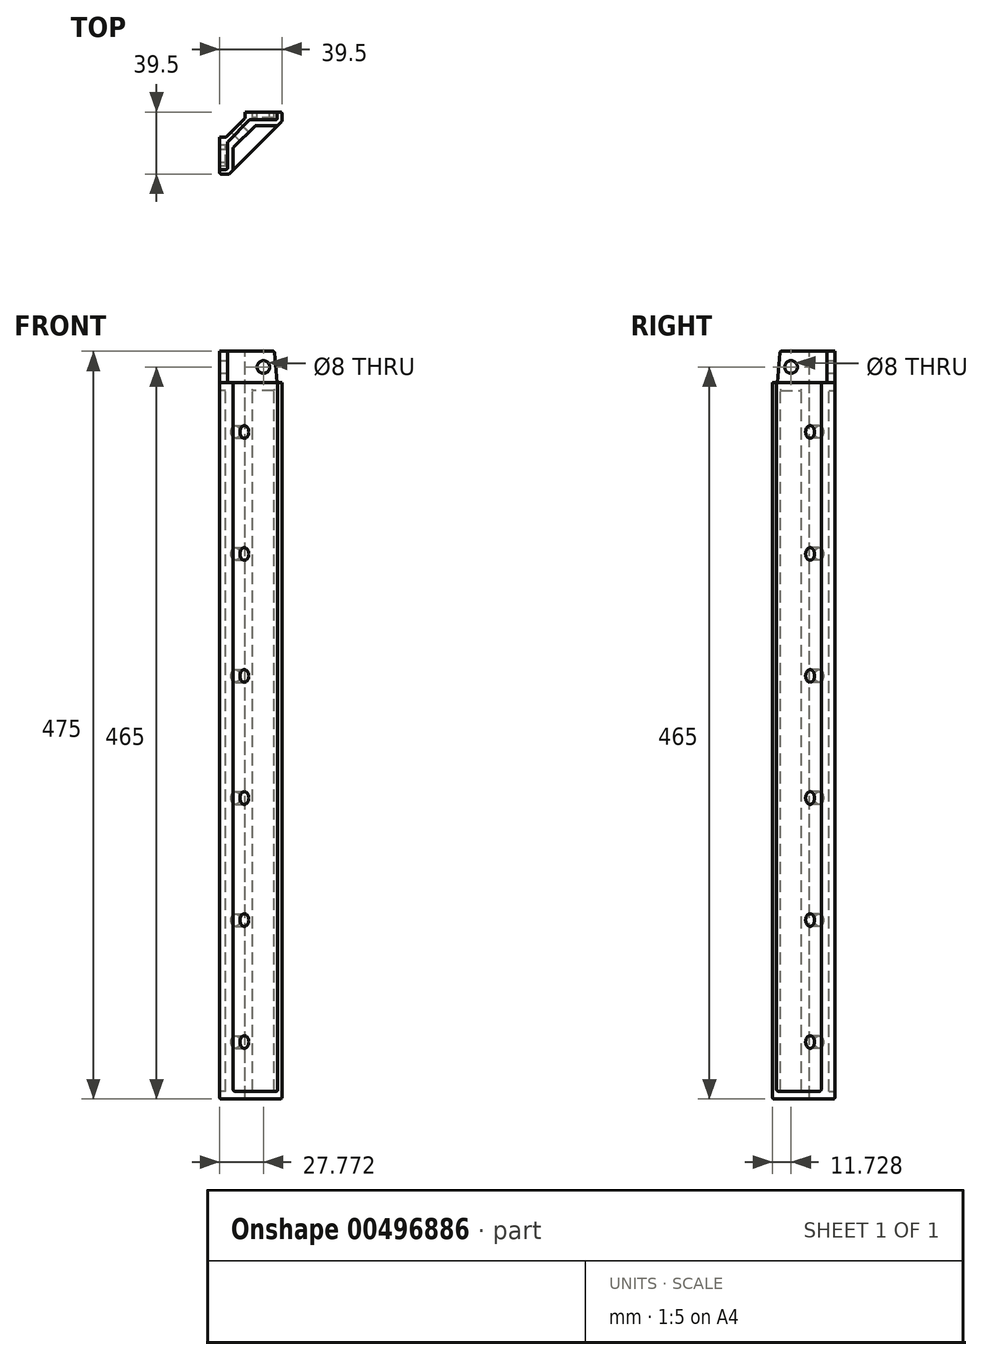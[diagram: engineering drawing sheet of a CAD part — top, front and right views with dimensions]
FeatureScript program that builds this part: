
annotation { "Feature Type Name" : "Feature", "Feature Type Description" : "" }
export const myFeature = defineFeature(function(context is Context, id is Id, definition is map)
    precondition{}
    {
        {
            var Q0;
            Q0=qCreatedBy(makeId("Top.planeOp"),FACE);
            var sketch = newSketch(context, id + "F0", { "sketchPlane" : qUnion([Q0])});
            skLineSegment(sketch, "E0", {"start": v(0, 30.13) * mm, "end": v(0, -27.95) * mm, "construction": true});
            skLineSegment(sketch, "E1", {"start": v(-25.65, 0) * mm, "end": v(27.57, 0) * mm, "construction": true});
            skLineSegment(sketch, "E2.bottom", {"start": v(-19.75, 19.75) * mm, "end": v(19.75, 19.75) * mm});
            skLineSegment(sketch, "E2.top", {"start": v(-19.75, -19.75) * mm, "end": v(-13.75, -19.75) * mm});
            skLineSegment(sketch, "E2.left", {"start": v(-19.75, 19.75) * mm, "end": v(-19.75, -19.75) * mm});
            skLineSegment(sketch, "E2.right", {"start": v(19.75, 19.75) * mm, "end": v(19.75, 13.75) * mm});
            skLineSegment(sketch, "E3", {"start": v(-13.75, -19.75) * mm, "end": v(19.75, 13.75) * mm});
            skSolve(sketch);
        }
        {
            var Q0;
            Q0=qSketchRegion(id+"F0",true);
            extrude(context, id + "F1", {"entities" : qUnion([Q0]), "oppositeDirection" : true, "depth" : 455 * mm, "symmetric" : true});
        }
        {
            var Q0;
            Q0=makeQuery(id+"F1.opExtrude","CAP_FACE",FACE,{"disambiguationData":[OSD([sQuery(id+"F0.wireOp",EDGE,"E2.bottom"),sQuery(id+"F0.wireOp",EDGE,"E2.top"),sQuery(id+"F0.wireOp",EDGE,"E2.left"),sQuery(id+"F0.wireOp",EDGE,"E2.right"),sQuery(id+"F0.wireOp",EDGE,"E3")])],"isStart":true});
            var sketch = newSketch(context, id + "F2", { "sketchPlane" : qUnion([Q0])});
            skLineSegment(sketch, "E4", {"start": v(3, -3) * mm, "end": v(-19.75, 19.75) * mm, "construction": true});
            skLineSegment(sketch, "E5", {"start": v(3, -3) * mm, "end": v(17.14, 11.14) * mm});
            skLineSegment(sketch, "E6", {"start": v(3, -3) * mm, "end": v(-11.14, -17.14) * mm});
            skLineSegment(sketch, "E7", {"start": v(-11.14, -3) * mm, "end": v(3, 11.14) * mm});
            skLineSegment(sketch, "E8", {"start": v(-11.14, -17.14) * mm, "end": v(-11.14, -3) * mm});
            skLineSegment(sketch, "E9", {"start": v(3, 11.14) * mm, "end": v(17.14, 11.14) * mm});
            skSolve(sketch);
        }
        {
            var Q0;
            Q0=qSketchRegion(id+"F2",true);
            extrude(context, id + "F3", {"entities" : qUnion([Q0]), "operationType" : NewBodyOperationType.REMOVE, "oppositeDirection" : true, "depth" : 450 * mm});
        }
        {
            var Q0;
            Q0=makeQuery(id+"F1.opExtrude","CAP_FACE",FACE,{"disambiguationData":[OSD([sQuery(id+"F0.wireOp",EDGE,"E2.bottom"),sQuery(id+"F0.wireOp",EDGE,"E2.top"),sQuery(id+"F0.wireOp",EDGE,"E2.left"),sQuery(id+"F0.wireOp",EDGE,"E2.right"),sQuery(id+"F0.wireOp",EDGE,"E3")])],"isStart":true});
            var sketch = newSketch(context, id + "F4", { "sketchPlane" : qUnion([Q0])});
            skPoint(sketch, "E10.orphan", {"position": v(-19.75, -19.75) * mm});
            skPoint(sketch, "E11.orphan", {"position": v(19.75, 19.75) * mm});
            skLineSegment(sketch, "E12", {"start": v(-19.75, 19.75) * mm, "end": v(-4.07, 4.07) * mm, "construction": true});
            skLineSegment(sketch, "E13", {"start": v(-15.75, 3.7) * mm, "end": v(-19.75, 3.7) * mm});
            skLineSegment(sketch, "E14", {"start": v(-3.7, 15.75) * mm, "end": v(-3.7, 19.75) * mm});
            skLineSegment(sketch, "E15", {"start": v(-3.7, 19.75) * mm, "end": v(-19.75, 19.75) * mm});
            skLineSegment(sketch, "E16", {"start": v(-19.75, 19.75) * mm, "end": v(-19.75, 3.7) * mm});
            skLineSegment(sketch, "E17", {"start": v(-3.7, 15.75) * mm, "end": v(-15.75, 3.7) * mm});
            skPoint(sketch, "E18.orphan", {"position": v(-14.68, 3.7) * mm});
            skPoint(sketch, "E19.orphan", {"position": v(-3.7, 13.6) * mm});
            skSolve(sketch);
        }
        {
            var Q0;
            Q0=qSketchRegion(id+"F4",true);
            extrude(context, id + "F5", {"entities" : qUnion([Q0]), "operationType" : NewBodyOperationType.REMOVE, "endBound" : BoundingType.THROUGH_ALL, "oppositeDirection" : true, "depth" : 25 * mm});
        }
        {
            var Q0;
            Q0=makeQuery(id+"F1.opExtrude","CAP_FACE",FACE,{"disambiguationData":[OSD([sQuery(id+"F0.wireOp",EDGE,"E2.bottom"),sQuery(id+"F0.wireOp",EDGE,"E2.top"),sQuery(id+"F0.wireOp",EDGE,"E2.left"),sQuery(id+"F0.wireOp",EDGE,"E2.right"),sQuery(id+"F0.wireOp",EDGE,"E3")])],"isStart":true});
            var sketch = newSketch(context, id + "F6", { "sketchPlane" : qUnion([Q0])});
            skLineSegment(sketch, "E20.0", {"start": v(1.3, 16.14) * mm, "end": v(14.75, 16.14) * mm});
            skLineSegment(sketch, "E20.1", {"start": v(14.75, 19.75) * mm, "end": v(14.75, 16.14) * mm});
            skLineSegment(sketch, "E21.0", {"start": v(1.3, 16.14) * mm, "end": v(1.3, 19.75) * mm});
            skLineSegment(sketch, "E22", {"start": v(14.75, 19.75) * mm, "end": v(1.3, 19.75) * mm});
            skLineSegment(sketch, "E23.0", {"start": v(-16.14, -14.75) * mm, "end": v(-16.14, -1.3) * mm});
            skLineSegment(sketch, "E23.1", {"start": v(-19.75, -14.75) * mm, "end": v(-16.14, -14.75) * mm});
            skLineSegment(sketch, "E24.0", {"start": v(-16.14, -1.3) * mm, "end": v(-19.75, -1.3) * mm});
            skPoint(sketch, "E25.orphan", {"position": v(-12.53, -1.3) * mm});
            skLineSegment(sketch, "E26", {"start": v(-19.75, -14.75) * mm, "end": v(-19.75, -1.3) * mm});
            skSolve(sketch);
        }
        {
            var Q0;
            Q0=qSketchRegion(id+"F6",true);
            extrude(context, id + "F7", {"entities" : qUnion([Q0]), "operationType" : NewBodyOperationType.REMOVE, "endBound" : BoundingType.THROUGH_ALL, "oppositeDirection" : true, "depth" : 25 * mm});
        }
        {
            var Q0;
            {var subQ1=sQuery(id+"F0.wireOp",EDGE,"E2.right");var subQ4=sQuery(id+"F0.wireOp",EDGE,"E2.bottom");Q0=makeQuery(id+"F7.boolean.opBoolean","SPLIT",FACE,{"disambiguationData":[TD([makeQuery(id+"F1.opExtrude","SWEPT_FACE",FACE,{"disambiguationData":[OSD([subQ1])]})])],"derivedFrom":makeQuery(id+"F1.opExtrude","SWEPT_FACE",FACE,{"disambiguationData":[OSD([subQ4])]})});}
            var sketch = newSketch(context, id + "F8", { "sketchPlane" : qUnion([Q0])});
            skLineSegment(sketch, "E27.bottom", {"start": v(-14.75, 227.5) * mm, "end": v(-1.3, 227.5) * mm});
            skLineSegment(sketch, "E27.top", {"start": v(-14.75, 222.5) * mm, "end": v(-1.3, 222.5) * mm});
            skLineSegment(sketch, "E27.left", {"start": v(-14.75, 227.5) * mm, "end": v(-14.75, 222.5) * mm});
            skLineSegment(sketch, "E27.right", {"start": v(-1.3, 227.5) * mm, "end": v(-1.3, 222.5) * mm});
            skLineSegment(sketch, "E28.bottom", {"start": v(-14.75, -227.5) * mm, "end": v(-1.3, -227.5) * mm});
            skLineSegment(sketch, "E28.top", {"start": v(-14.75, -222.5) * mm, "end": v(-1.3, -222.5) * mm});
            skLineSegment(sketch, "E28.left", {"start": v(-14.75, -227.5) * mm, "end": v(-14.75, -222.5) * mm});
            skLineSegment(sketch, "E28.right", {"start": v(-1.3, -227.5) * mm, "end": v(-1.3, -222.5) * mm});
            skSolve(sketch);
        }
        {
            var Q0;
            Q0=qSketchRegion(id+"F8",true);
            var Q1;
            Q1=makeQuery(id+"F7.boolean.opBoolean","COPY",FACE,{"derivedFrom":makeQuery(id+"F7.opExtrude","SWEPT_FACE",FACE,{"disambiguationData":[OSD([sQuery(id+"F6.wireOp",EDGE,"E20.0")])]})});
            extrude(context, id + "F9", {"entities" : qUnion([Q0]), "operationType" : NewBodyOperationType.ADD, "endBound" : BoundingType.UP_TO_SURFACE, "oppositeDirection" : true, "endBoundEntityFace" : qUnion([Q1]), "depth" : 25 * mm});
        }
        {
            var Q0;
            {var subQ2=sQuery(id+"F0.wireOp",EDGE,"E2.left");var subQ3=sQuery(id+"F0.wireOp",EDGE,"E2.top");Q0=makeQuery(id+"F7.boolean.opBoolean","SPLIT",FACE,{"disambiguationData":[TD([makeQuery(id+"F1.opExtrude","SWEPT_FACE",FACE,{"disambiguationData":[OSD([subQ3])]})])],"derivedFrom":makeQuery(id+"F1.opExtrude","SWEPT_FACE",FACE,{"disambiguationData":[OSD([subQ2])]})});}
            var sketch = newSketch(context, id + "F10", { "sketchPlane" : qUnion([Q0])});
            skLineSegment(sketch, "E29.bottom", {"start": v(14.75, 227.5) * mm, "end": v(1.3, 227.5) * mm});
            skLineSegment(sketch, "E29.top", {"start": v(14.75, 222.5) * mm, "end": v(1.3, 222.5) * mm});
            skLineSegment(sketch, "E29.left", {"start": v(14.75, 227.5) * mm, "end": v(14.75, 222.5) * mm});
            skLineSegment(sketch, "E29.right", {"start": v(1.3, 227.5) * mm, "end": v(1.3, 222.5) * mm});
            skLineSegment(sketch, "E30.bottom", {"start": v(14.75, -227.5) * mm, "end": v(1.3, -227.5) * mm});
            skLineSegment(sketch, "E30.top", {"start": v(14.75, -222.5) * mm, "end": v(1.3, -222.5) * mm});
            skLineSegment(sketch, "E30.left", {"start": v(14.75, -227.5) * mm, "end": v(14.75, -222.5) * mm});
            skLineSegment(sketch, "E30.right", {"start": v(1.3, -227.5) * mm, "end": v(1.3, -222.5) * mm});
            skSolve(sketch);
        }
        {
            var Q0;
            Q0=qSketchRegion(id+"F10",true);
            var Q1;
            Q1=makeQuery(id+"F7.boolean.opBoolean","COPY",FACE,{"derivedFrom":makeQuery(id+"F7.opExtrude","SWEPT_FACE",FACE,{"disambiguationData":[OSD([sQuery(id+"F6.wireOp",EDGE,"E23.0")])]})});
            extrude(context, id + "F11", {"entities" : qUnion([Q0]), "operationType" : NewBodyOperationType.ADD, "endBound" : BoundingType.UP_TO_SURFACE, "oppositeDirection" : true, "endBoundEntityFace" : qUnion([Q1]), "depth" : 25 * mm});
        }
        {
            var Q0;
            {var subQ2=sQuery(id+"F0.wireOp",EDGE,"E2.left");var subQ3=sQuery(id+"F0.wireOp",EDGE,"E2.top");var subQ7=makeQuery(id+"F1.opExtrude","SWEPT_FACE",FACE,{"disambiguationData":[OSD([subQ2])]});Q0=makeQuery(id+"F11.boolean.opBoolean","MERGE",FACE,{"derivedFrom":[makeQuery(id+"F7.boolean.opBoolean","SPLIT",FACE,{"disambiguationData":[TD([makeQuery(id+"F1.opExtrude","SWEPT_FACE",FACE,{"disambiguationData":[OSD([subQ3])]})])],"derivedFrom":subQ7}),makeQuery(id+"F7.boolean.opBoolean","SPLIT",FACE,{"disambiguationData":[TD([makeQuery(id+"F5.boolean.opBoolean","COPY",FACE,{"derivedFrom":makeQuery(id+"F5.opExtrude","SWEPT_FACE",FACE,{"disambiguationData":[OSD([sQuery(id+"F4.wireOp",EDGE,"E13")])]})})])],"derivedFrom":subQ7}),makeQuery(id+"F11.opExtrude","CAP_FACE",FACE,{"disambiguationData":[OSD([sQuery(id+"F10.wireOp",EDGE,"E29.bottom"),sQuery(id+"F10.wireOp",EDGE,"E29.top"),sQuery(id+"F10.wireOp",EDGE,"E29.left"),sQuery(id+"F10.wireOp",EDGE,"E29.right")])],"isStart":true}),makeQuery(id+"F11.opExtrude","CAP_FACE",FACE,{"disambiguationData":[OSD([sQuery(id+"F10.wireOp",EDGE,"E30.bottom"),sQuery(id+"F10.wireOp",EDGE,"E30.top"),sQuery(id+"F10.wireOp",EDGE,"E30.left"),sQuery(id+"F10.wireOp",EDGE,"E30.right")])],"isStart":true})]});}
            var sketch = newSketch(context, id + "F12", { "sketchPlane" : qUnion([Q0])});
            skLineSegment(sketch, "E31", {"start": v(8.02, 227.5) * mm, "end": v(8.02, 247.5) * mm, "construction": true});
            skLineSegment(sketch, "E32", {"start": v(0, 0) * mm, "end": v(35.4, 0) * mm, "construction": true});
            skPoint(sketch, "E32.endSnap0", {"position": v(19.75, 0) * mm});
            skLineSegment(sketch, "E33.MirrorCS", {"start": v(16.04, 0) * mm, "end": v(-19.35, 0) * mm, "construction": true});
            skLineSegment(sketch, "E34", {"start": v(16.75, 227.5) * mm, "end": v(-0.7, 227.5) * mm});
            skLineSegment(sketch, "E35", {"start": v(16.75, 227.5) * mm, "end": v(15.02, 247.5) * mm});
            skLineSegment(sketch, "E36", {"start": v(15.02, 247.5) * mm, "end": v(8.02, 247.5) * mm});
            skLineSegment(sketch, "E37", {"start": v(8.02, 247.5) * mm, "end": v(1.02, 247.5) * mm});
            skLineSegment(sketch, "E38", {"start": v(1.02, 247.5) * mm, "end": v(-0.7, 227.5) * mm});
            skLineSegment(sketch, "E39.MirrorCS", {"start": v(-0.7, 227.5) * mm, "end": v(1.02, 247.5) * mm});
            skSolve(sketch);
        }
        {
            var Q0;
            Q0=qSketchRegion(id+"F12",true);
            extrude(context, id + "F13", {"entities" : qUnion([Q0]), "operationType" : NewBodyOperationType.ADD, "oppositeDirection" : true, "depth" : 5 * mm});
        }
        {
            var Q0;
            {var subQ1=sQuery(id+"F0.wireOp",EDGE,"E2.right");var subQ4=sQuery(id+"F0.wireOp",EDGE,"E2.bottom");var subQ7=makeQuery(id+"F1.opExtrude","SWEPT_FACE",FACE,{"disambiguationData":[OSD([subQ4])]});Q0=makeQuery(id+"F9.boolean.opBoolean","MERGE",FACE,{"derivedFrom":[makeQuery(id+"F7.boolean.opBoolean","SPLIT",FACE,{"disambiguationData":[TD([makeQuery(id+"F1.opExtrude","SWEPT_FACE",FACE,{"disambiguationData":[OSD([subQ1])]})])],"derivedFrom":subQ7}),makeQuery(id+"F7.boolean.opBoolean","SPLIT",FACE,{"disambiguationData":[TD([makeQuery(id+"F5.boolean.opBoolean","COPY",FACE,{"derivedFrom":makeQuery(id+"F5.opExtrude","SWEPT_FACE",FACE,{"disambiguationData":[OSD([sQuery(id+"F4.wireOp",EDGE,"E14")])]})})])],"derivedFrom":subQ7}),makeQuery(id+"F9.opExtrude","CAP_FACE",FACE,{"disambiguationData":[OSD([sQuery(id+"F8.wireOp",EDGE,"E27.bottom"),sQuery(id+"F8.wireOp",EDGE,"E27.top"),sQuery(id+"F8.wireOp",EDGE,"E27.left"),sQuery(id+"F8.wireOp",EDGE,"E27.right")])],"isStart":true}),makeQuery(id+"F9.opExtrude","CAP_FACE",FACE,{"disambiguationData":[OSD([sQuery(id+"F8.wireOp",EDGE,"E28.bottom"),sQuery(id+"F8.wireOp",EDGE,"E28.top"),sQuery(id+"F8.wireOp",EDGE,"E28.left"),sQuery(id+"F8.wireOp",EDGE,"E28.right")])],"isStart":true})]});}
            var sketch = newSketch(context, id + "F14", { "sketchPlane" : qUnion([Q0])});
            skLineSegment(sketch, "E40", {"start": v(-8.02, 227.5) * mm, "end": v(-8.02, 247.66) * mm, "construction": true});
            skPoint(sketch, "E40.endSnap0", {"position": v(-8.02, 227.5) * mm});
            skLineSegment(sketch, "E41", {"start": v(-15.02, 247.5) * mm, "end": v(-1.02, 247.5) * mm});
            skLineSegment(sketch, "E42", {"start": v(0, 0) * mm, "end": v(-60.6, 0) * mm, "construction": true});
            skPoint(sketch, "E42.endSnap0", {"position": v(-14.75, 0) * mm});
            skLineSegment(sketch, "E43", {"start": v(-15.02, 247.5) * mm, "end": v(-16.75, 227.5) * mm});
            skLineSegment(sketch, "E44", {"start": v(-1.02, 247.5) * mm, "end": v(0.7, 227.5) * mm});
            skLineSegment(sketch, "E45", {"start": v(0.7, 227.5) * mm, "end": v(-16.75, 227.5) * mm});
            skSolve(sketch);
        }
        {
            var Q0;
            Q0=qSketchRegion(id+"F14",true);
            extrude(context, id + "F15", {"entities" : qUnion([Q0]), "operationType" : NewBodyOperationType.ADD, "oppositeDirection" : true, "depth" : 5 * mm});
        }
        {
            var Q0;
            {var subQ1=sQuery(id+"F0.wireOp",EDGE,"E2.right");var subQ4=sQuery(id+"F0.wireOp",EDGE,"E2.bottom");var subQ7=makeQuery(id+"F1.opExtrude","SWEPT_FACE",FACE,{"disambiguationData":[OSD([subQ4])]});Q0=makeQuery(id+"F15.boolean.opBoolean","MERGE",FACE,{"derivedFrom":[makeQuery(id+"F9.boolean.opBoolean","MERGE",FACE,{"derivedFrom":[makeQuery(id+"F7.boolean.opBoolean","SPLIT",FACE,{"disambiguationData":[TD([makeQuery(id+"F1.opExtrude","SWEPT_FACE",FACE,{"disambiguationData":[OSD([subQ1])]})])],"derivedFrom":subQ7}),makeQuery(id+"F7.boolean.opBoolean","SPLIT",FACE,{"disambiguationData":[TD([makeQuery(id+"F5.boolean.opBoolean","COPY",FACE,{"derivedFrom":makeQuery(id+"F5.opExtrude","SWEPT_FACE",FACE,{"disambiguationData":[OSD([sQuery(id+"F4.wireOp",EDGE,"E14")])]})})])],"derivedFrom":subQ7}),makeQuery(id+"F9.opExtrude","CAP_FACE",FACE,{"disambiguationData":[OSD([sQuery(id+"F8.wireOp",EDGE,"E27.bottom"),sQuery(id+"F8.wireOp",EDGE,"E27.top"),sQuery(id+"F8.wireOp",EDGE,"E27.left"),sQuery(id+"F8.wireOp",EDGE,"E27.right")])],"isStart":true}),makeQuery(id+"F9.opExtrude","CAP_FACE",FACE,{"disambiguationData":[OSD([sQuery(id+"F8.wireOp",EDGE,"E28.bottom"),sQuery(id+"F8.wireOp",EDGE,"E28.top"),sQuery(id+"F8.wireOp",EDGE,"E28.left"),sQuery(id+"F8.wireOp",EDGE,"E28.right")])],"isStart":true})]}),makeQuery(id+"F15.opExtrude","CAP_FACE",FACE,{"disambiguationData":[OSD([sQuery(id+"F14.wireOp",EDGE,"AjdLOBUI-PND2-HRux-vW9i-I60BuJFxOAxo"),sQuery(id+"F14.wireOp",EDGE,"m2E0O1S7-ugW4-w8lP-xUBK-8UGrL3XVD3p1"),sQuery(id+"F14.wireOp",EDGE,"E41"),sQuery(id+"F14.wireOp",EDGE,"z751VbyZ-Eswl-sp4i-D6d8-2ebrKqnJ25gN")])],"isStart":true}),makeQuery(id+"F15.opExtrude","CAP_FACE",FACE,{"disambiguationData":[OSD([sQuery(id+"F14.wireOp",EDGE,"9fced805-f766-4b14-a849-f1590210c0c81.MirrorCS"),sQuery(id+"F14.wireOp",EDGE,"9fced805-f766-4b14-a849-f1590210c0c82.MirrorCS"),sQuery(id+"F14.wireOp",EDGE,"9fced805-f766-4b14-a849-f1590210c0c83.MirrorCS"),sQuery(id+"F14.wireOp",EDGE,"9fced805-f766-4b14-a849-f1590210c0c84.MirrorCS")])],"isStart":true})]});}
            var sketch = newSketch(context, id + "F16", { "sketchPlane" : qUnion([Q0])});
            skLineSegment(sketch, "E46", {"start": v(-8.02, 247.5) * mm, "end": v(-8.02, 8.86) * mm, "construction": true});
            skCircle(sketch, "E47", {"center": v(-8.02, 237.5) * mm, "radius": 4 * mm});
            skSolve(sketch);
        }
        {
            var Q0;
            Q0=qSketchRegion(id+"F16",true);
            extrude(context, id + "F17", {"entities" : qUnion([Q0]), "operationType" : NewBodyOperationType.REMOVE, "endBound" : BoundingType.THROUGH_ALL, "oppositeDirection" : true, "depth" : 25 * mm});
        }
        {
            var Q0;
            Q0=makeQuery(id+"F3.boolean.opBoolean","COPY",FACE,{"derivedFrom":makeQuery(id+"F3.opExtrude","SWEPT_FACE",FACE,{"disambiguationData":[OSD([sQuery(id+"F2.wireOp",EDGE,"E7")])]})});
            var sketch = newSketch(context, id + "F18", { "sketchPlane" : qUnion([Q0])});
            skLineSegment(sketch, "E48", {"start": v(0, 227.5) * mm, "end": v(0, -222.5) * mm, "construction": true});
            skLineSegment(sketch, "E49", {"start": v(0, 2.5) * mm, "end": v(10, 2.5) * mm, "construction": true});
            skCircle(sketch, "E50", {"center": v(0, 196.25) * mm, "radius": 4 * mm});
            skCircle(sketch, "E51", {"center": v(0, 118.75) * mm, "radius": 4 * mm});
            skCircle(sketch, "E52.MirrorC", {"center": v(0, -191.25) * mm, "radius": 4 * mm});
            skCircle(sketch, "E53.MirrorC", {"center": v(0, -113.75) * mm, "radius": 4 * mm});
            skCircle(sketch, "E54", {"center": v(0, 41.25) * mm, "radius": 4 * mm});
            skCircle(sketch, "E55.MirrorC", {"center": v(0, -36.25) * mm, "radius": 4 * mm});
            skSolve(sketch);
        }
        {
            var Q0;
            Q0=qSketchRegion(id+"F18",true);
            extrude(context, id + "F19", {"entities" : qUnion([Q0]), "operationType" : NewBodyOperationType.REMOVE, "endBound" : BoundingType.THROUGH_ALL, "oppositeDirection" : true, "depth" : 25 * mm});
        }
        {
            var Q0;
            Q0=makeQuery(id+"F13.opExtrude","CAP_FACE",FACE,{"disambiguationData":[OSD([sQuery(id+"F12.wireOp",EDGE,"E34"),sQuery(id+"F12.wireOp",EDGE,"E35"),sQuery(id+"F12.wireOp",EDGE,"E36"),sQuery(id+"F12.wireOp",EDGE,"E37"),sQuery(id+"F12.wireOp",EDGE,"E39.MirrorCS")])],"isStart":false});
            var sketch = newSketch(context, id + "F20", { "sketchPlane" : qUnion([Q0])});
            skLineSegment(sketch, "E56", {"start": v(-8.02, 247.5) * mm, "end": v(-8.02, 52.5) * mm, "construction": true});
            skPoint(sketch, "E56.endSnap0", {"position": v(-8.02, 247.5) * mm});
            skCircle(sketch, "E57", {"center": v(-8.02, 237.5) * mm, "radius": 4 * mm});
            skSolve(sketch);
        }
        {
            var Q0;
            Q0=qSketchRegion(id+"F20",true);
            extrude(context, id + "F21", {"entities" : qUnion([Q0]), "operationType" : NewBodyOperationType.REMOVE, "endBound" : BoundingType.THROUGH_ALL, "oppositeDirection" : true, "depth" : 25 * mm});
        }
        {
            var Q0;
            Q0=makeQuery(id+"F11.boolean.opBoolean","MERGE",FACE,{"derivedFrom":[makeQuery(id+"F9.boolean.opBoolean","MERGE",FACE,{"derivedFrom":[makeQuery(id+"F1.opExtrude","CAP_FACE",FACE,{"disambiguationData":[OSD([sQuery(id+"F0.wireOp",EDGE,"E2.bottom"),sQuery(id+"F0.wireOp",EDGE,"E2.top"),sQuery(id+"F0.wireOp",EDGE,"E2.left"),sQuery(id+"F0.wireOp",EDGE,"E2.right"),sQuery(id+"F0.wireOp",EDGE,"E3")])],"isStart":true}),makeQuery(id+"F9.opExtrude","SWEPT_FACE",FACE,{"disambiguationData":[OSD([sQuery(id+"F8.wireOp",EDGE,"E27.bottom")])]})]}),makeQuery(id+"F11.opExtrude","SWEPT_FACE",FACE,{"disambiguationData":[OSD([sQuery(id+"F10.wireOp",EDGE,"E29.bottom")])]})]});
            var sketch = newSketch(context, id + "F22", { "sketchPlane" : qUnion([Q0])});
            skLineSegment(sketch, "E58.0", {"start": v(-0.7, 14.75) * mm, "end": v(-0.7, 19.75) * mm});
            skPoint(sketch, "E59.0", {"position": v(-2.2, 19.75) * mm});
            skLineSegment(sketch, "E60.0", {"start": v(-3.7, 19.75) * mm, "end": v(-0.7, 19.75) * mm});
            skLineSegment(sketch, "E61.0", {"start": v(-3.7, 15.75) * mm, "end": v(-3.7, 19.75) * mm});
            skLineSegment(sketch, "E62.0", {"start": v(-3.7, 15.75) * mm, "end": v(-15.75, 3.7) * mm});
            skLineSegment(sketch, "E63.0", {"start": v(-15.75, 3.7) * mm, "end": v(-19.75, 3.7) * mm});
            skLineSegment(sketch, "E64.0", {"start": v(-19.75, 3.7) * mm, "end": v(-19.75, 0.7) * mm});
            skLineSegment(sketch, "E65.0", {"start": v(-14.75, 0.7) * mm, "end": v(-19.75, 0.7) * mm});
            skPoint(sketch, "E66.orphan", {"position": v(1.02, 14.75) * mm});
            skLineSegment(sketch, "E67", {"start": v(-14.75, 0.7) * mm, "end": v(-0.7, 14.75) * mm});
            skSolve(sketch);
        }
        {
            var Q0;
            Q0 = qSketchRegion(id + "F22", true);
            extrude(context, id + "F23", {"entities" : qUnion([Q0]), "operationType" : NewBodyOperationType.ADD, "depth" : 20 * mm});
        }
        {
            var Q0;
            Q0=makeQuery(id+"F13.opExtrude","SWEPT_FACE",FACE,{"disambiguationData":[OSD([sQuery(id+"F12.wireOp",EDGE,"E36"),sQuery(id+"F12.wireOp",EDGE,"E37")])]});
            var sketch = newSketch(context, id + "F24", { "sketchPlane" : qUnion([Q0])});
            skLineSegment(sketch, "E68.0.0", {"start": v(-19.75, 0.7) * mm, "end": v(-19.75, -1.02) * mm});
            skLineSegment(sketch, "E68.0.1", {"start": v(-19.75, -1.02) * mm, "end": v(-14.75, -1.02) * mm});
            skLineSegment(sketch, "E68.0.2", {"start": v(-14.75, -1.02) * mm, "end": v(-14.75, 0.7) * mm});
            skLineSegment(sketch, "E68.0.3", {"start": v(-14.75, 0.7) * mm, "end": v(-19.75, 0.7) * mm});
            skLineSegment(sketch, "E69.0.0", {"start": v(1.02, 19.75) * mm, "end": v(-0.7, 19.75) * mm});
            skLineSegment(sketch, "E69.0.1", {"start": v(-0.7, 19.75) * mm, "end": v(-0.7, 14.75) * mm});
            skLineSegment(sketch, "E69.0.2", {"start": v(-0.7, 14.75) * mm, "end": v(1.02, 14.75) * mm});
            skLineSegment(sketch, "E69.0.3", {"start": v(1.02, 14.75) * mm, "end": v(1.02, 19.75) * mm});
            skSolve(sketch);
        }
        {
            var Q0;
            Q0 = qSketchRegion(id + "F24", true);
            extrude(context, id + "F25", {"entities" : qUnion([Q0]), "operationType" : NewBodyOperationType.ADD, "oppositeDirection" : true, "depth" : 25 * mm});
        }
        {
            var Q0;
            Q0=makeQuery(id+"F13.opExtrude","SWEPT_EDGE",EDGE,{"disambiguationData":[OSD([sQuery(id+"F12.wireOp",EDGE,"E35"),sQuery(id+"F12.wireOp",EDGE,"E36")])]});
            var Q1;
            Q1=makeQuery(id+"F13.opExtrude","SWEPT_EDGE",EDGE,{"disambiguationData":[OSD([sQuery(id+"F12.wireOp",EDGE,"E37"),sQuery(id+"F12.wireOp",EDGE,"E39.MirrorCS")])]});
            var Q2;
            Q2=makeQuery(id+"F15.opExtrude","SWEPT_EDGE",EDGE,{"disambiguationData":[OSD([sQuery(id+"F14.wireOp",EDGE,"E41"),sQuery(id+"F14.wireOp",EDGE,"E43")])]});
            var Q3;
            Q3=makeQuery(id+"F15.opExtrude","SWEPT_EDGE",EDGE,{"disambiguationData":[OSD([sQuery(id+"F14.wireOp",EDGE,"E41"),sQuery(id+"F14.wireOp",EDGE,"E44")])]});
            var Q4;
            Q4=makeQuery(id+"F15.opExtrude","SWEPT_EDGE",EDGE,{"disambiguationData":[OSD([sQuery(id+"F14.wireOp",EDGE,"14d68a54-c34f-48c8-ae77-41faf57796821.MirrorCS"),sQuery(id+"F14.wireOp",EDGE,"14d68a54-c34f-48c8-ae77-41faf57796823.MirrorCS")])]});
            var Q5;
            Q5=makeQuery(id+"F15.opExtrude","SWEPT_EDGE",EDGE,{"disambiguationData":[OSD([sQuery(id+"F14.wireOp",EDGE,"14d68a54-c34f-48c8-ae77-41faf57796820.MirrorCS"),sQuery(id+"F14.wireOp",EDGE,"14d68a54-c34f-48c8-ae77-41faf57796823.MirrorCS")])]});
            var Q6;
            Q6=makeQuery(id+"F13.opExtrude","SWEPT_EDGE",EDGE,{"disambiguationData":[OSD([sQuery(id+"F12.wireOp",EDGE,"0e25475b-3a4a-4502-b2ef-1a4ccfbb12351.MirrorCS"),sQuery(id+"F12.wireOp",EDGE,"0e25475b-3a4a-4502-b2ef-1a4ccfbb12353.MirrorCS")])]});
            var Q7;
            Q7=makeQuery(id+"F13.opExtrude","SWEPT_EDGE",EDGE,{"disambiguationData":[OSD([sQuery(id+"F12.wireOp",EDGE,"0e25475b-3a4a-4502-b2ef-1a4ccfbb12352.MirrorCS"),sQuery(id+"F12.wireOp",EDGE,"0e25475b-3a4a-4502-b2ef-1a4ccfbb12353.MirrorCS")])]});
            var Q8;
            Q8=makeQuery(id+"F1.opExtrude","SWEPT_EDGE",EDGE,{"disambiguationData":[OSD([sQuery(id+"F0.wireOp",EDGE,"E2.top"),sQuery(id+"F0.wireOp",EDGE,"E3")])]});
            var Q9;
            Q9=makeQuery(id+"F1.opExtrude","SWEPT_EDGE",EDGE,{"disambiguationData":[OSD([sQuery(id+"F0.wireOp",EDGE,"E2.right"),sQuery(id+"F0.wireOp",EDGE,"E3")])]});
            var Q10;
            Q10=makeQuery(id+"F3.boolean.opBoolean","COPY",EDGE,{"derivedFrom":makeQuery(id+"F3.opExtrude","SWEPT_EDGE",EDGE,{"disambiguationData":[OSD([sQuery(id+"F2.wireOp",EDGE,"E7"),sQuery(id+"F2.wireOp",EDGE,"E8")])]})});
            var Q11;
            Q11=makeQuery(id+"F3.boolean.opBoolean","COPY",EDGE,{"derivedFrom":makeQuery(id+"F3.opExtrude","SWEPT_EDGE",EDGE,{"disambiguationData":[OSD([sQuery(id+"F2.wireOp",EDGE,"E7"),sQuery(id+"F2.wireOp",EDGE,"E9")])]})});
            var Q12;
            Q12=makeQuery(id+"F5.boolean.opBoolean","COPY",EDGE,{"derivedFrom":makeQuery(id+"F5.opExtrude","SWEPT_EDGE",EDGE,{"disambiguationData":[OSD([sQuery(id+"F4.wireOp",EDGE,"E13"),sQuery(id+"F4.wireOp",EDGE,"E17")])]})});
            var Q13;
            Q13=makeQuery(id+"F5.boolean.opBoolean","COPY",EDGE,{"derivedFrom":makeQuery(id+"F5.opExtrude","SWEPT_EDGE",EDGE,{"disambiguationData":[OSD([sQuery(id+"F4.wireOp",EDGE,"E14"),sQuery(id+"F4.wireOp",EDGE,"E17")])]})});
            var Q14;
            Q14=makeQuery(id+"F5.boolean.opBoolean","COPY",EDGE,{"derivedFrom":makeQuery(id+"F5.opExtrude","SWEPT_EDGE",EDGE,{"disambiguationData":[OSD([sQuery(id+"F0.wireOp",EDGE,"E2.bottom"),sQuery(id+"F4.wireOp",EDGE,"E14"),sQuery(id+"F4.wireOp",EDGE,"E15")])]})});
            var Q15;
            Q15=makeQuery(id+"F5.boolean.opBoolean","COPY",EDGE,{"derivedFrom":makeQuery(id+"F5.opExtrude","SWEPT_EDGE",EDGE,{"disambiguationData":[OSD([sQuery(id+"F0.wireOp",EDGE,"E2.left"),sQuery(id+"F4.wireOp",EDGE,"E13"),sQuery(id+"F4.wireOp",EDGE,"E16")])]})});
            var Q16;
            Q16=makeQuery(id+"F11.opExtrude","SWEPT_EDGE",EDGE,{"disambiguationData":[OSD([sQuery(id+"F0.wireOp",EDGE,"E2.left"),sQuery(id+"F6.wireOp",EDGE,"E23.1"),sQuery(id+"F6.wireOp",EDGE,"E26"),sQuery(id+"F10.wireOp",EDGE,"E29.top"),sQuery(id+"F10.wireOp",EDGE,"E29.left")])]});
            var Q17;
            Q17=makeQuery(id+"F11.opExtrude","SWEPT_EDGE",EDGE,{"disambiguationData":[OSD([sQuery(id+"F10.wireOp",EDGE,"E29.top"),sQuery(id+"F10.wireOp",EDGE,"E29.right")])]});
            var Q18;
            Q18=makeQuery(id+"F11.opExtrude","SWEPT_EDGE",EDGE,{"disambiguationData":[OSD([sQuery(id+"F10.wireOp",EDGE,"E30.top"),sQuery(id+"F10.wireOp",EDGE,"E30.right")])]});
            var Q19;
            Q19=makeQuery(id+"F11.opExtrude","SWEPT_EDGE",EDGE,{"disambiguationData":[OSD([sQuery(id+"F0.wireOp",EDGE,"E2.left"),sQuery(id+"F6.wireOp",EDGE,"E23.1"),sQuery(id+"F6.wireOp",EDGE,"E26"),sQuery(id+"F10.wireOp",EDGE,"E30.top"),sQuery(id+"F10.wireOp",EDGE,"E30.left")])]});
            var Q20;
            Q20=makeQuery(id+"F9.opExtrude","SWEPT_EDGE",EDGE,{"disambiguationData":[OSD([sQuery(id+"F0.wireOp",EDGE,"E2.bottom"),sQuery(id+"F6.wireOp",EDGE,"E20.1"),sQuery(id+"F6.wireOp",EDGE,"E22"),sQuery(id+"F8.wireOp",EDGE,"E28.top"),sQuery(id+"F8.wireOp",EDGE,"E28.left")])]});
            var Q21;
            Q21=makeQuery(id+"F9.opExtrude","SWEPT_EDGE",EDGE,{"disambiguationData":[OSD([sQuery(id+"F8.wireOp",EDGE,"E28.top"),sQuery(id+"F8.wireOp",EDGE,"E28.right")])]});
            var Q22;
            Q22=makeQuery(id+"F9.opExtrude","SWEPT_EDGE",EDGE,{"disambiguationData":[OSD([sQuery(id+"F0.wireOp",EDGE,"E2.bottom"),sQuery(id+"F6.wireOp",EDGE,"E20.1"),sQuery(id+"F6.wireOp",EDGE,"E22"),sQuery(id+"F8.wireOp",EDGE,"E27.top"),sQuery(id+"F8.wireOp",EDGE,"E27.left")])]});
            var Q23;
            Q23=makeQuery(id+"F9.opExtrude","SWEPT_EDGE",EDGE,{"disambiguationData":[OSD([sQuery(id+"F8.wireOp",EDGE,"E27.top"),sQuery(id+"F8.wireOp",EDGE,"E27.right")])]});
            var Q24;
            Q24=makeQuery(id+"FQgWeVVyTOw4oP8_1.1.F13.opExtrude","SWEPT_EDGE",EDGE,{"disambiguationData":[OSD([sQuery(id+"F12.wireOp",EDGE,"E35"),sQuery(id+"F12.wireOp",EDGE,"E36")])]});
            var Q25;
            Q25=makeQuery(id+"F0G2RlgfnTVtGBU_1.1.F15.opExtrude","SWEPT_EDGE",EDGE,{"disambiguationData":[OSD([sQuery(id+"F14.wireOp",EDGE,"E41"),sQuery(id+"F14.wireOp",EDGE,"E43")])]});
            var Q26;
            Q26=makeQuery(id+"FlFclubRB8u2xVJ_1.1.F23.opExtrude","SWEPT_EDGE",EDGE,{"disambiguationData":[OSD([sQuery(id+"F22.wireOp",EDGE,"13f4e866-1eac-4fd2-8cb8-b31731ec45be.0"),sQuery(id+"F22.wireOp",EDGE,"IEdAcdNN-kTPl-dZrz-dtDZ-8rgaU4BHqawl")])]});
            var Q27;
            Q27=makeQuery(id+"FlFclubRB8u2xVJ_1.1.F23.opExtrude","SWEPT_EDGE",EDGE,{"disambiguationData":[OSD([sQuery(id+"F22.wireOp",EDGE,"13f4e866-1eac-4fd2-8cb8-b31731ec45be.0"),sQuery(id+"F22.wireOp",EDGE,"EtFefJ2s-15CD-pvIh-Pjx4-gmoe8S5X5IGa")])]});
            var Q28;
            Q28=makeQuery(id+"F23.opExtrude","SWEPT_EDGE",EDGE,{"disambiguationData":[OSD([sQuery(id+"F22.wireOp",EDGE,"13f4e866-1eac-4fd2-8cb8-b31731ec45be.0"),sQuery(id+"F22.wireOp",EDGE,"EtFefJ2s-15CD-pvIh-Pjx4-gmoe8S5X5IGa")])]});
            var Q29;
            Q29=makeQuery(id+"F23.opExtrude","SWEPT_EDGE",EDGE,{"disambiguationData":[OSD([sQuery(id+"F22.wireOp",EDGE,"13f4e866-1eac-4fd2-8cb8-b31731ec45be.0"),sQuery(id+"F22.wireOp",EDGE,"IEdAcdNN-kTPl-dZrz-dtDZ-8rgaU4BHqawl")])]});
            fillet(context, id + "F26", {"entities" : qUnion([Q0, Q1, Q2, Q3, Q4, Q5, Q6, Q7, Q8, Q9, Q10, Q11, Q12, Q13, Q14, Q15, Q16, Q17, Q18, Q19, Q20, Q21, Q22, Q23, Q24, Q25, Q26, Q27, Q28, Q29]), "radius" : 1 * mm, "tangentPropagation" : true, "allowEdgeOverflow" : false});
        }
        {
            var Q0;
            Q0=makeQuery(id+"F25.opExtrude","SWEPT_EDGE",EDGE,{"disambiguationData":[OSD([sQuery(id+"F24.wireOp",EDGE,"E68.0.2"),sQuery(id+"F24.wireOp",EDGE,"E68.0.3")])]});
            var Q1;
            Q1=makeQuery(id+"F25.opExtrude","SWEPT_EDGE",EDGE,{"disambiguationData":[OSD([sQuery(id+"F24.wireOp",EDGE,"E69.0.1"),sQuery(id+"F24.wireOp",EDGE,"E69.0.2")])]});
            var Q2;
            Q2=makeQuery(id+"FP1PUGvhXahgOBu_1.1.F25.opExtrude","SWEPT_EDGE",EDGE,{"disambiguationData":[OSD([sQuery(id+"F24.wireOp",EDGE,"E68.0.2"),sQuery(id+"F24.wireOp",EDGE,"E68.0.3")])]});
            var Q3;
            Q3=makeQuery(id+"FP1PUGvhXahgOBu_1.1.F25.opExtrude","SWEPT_EDGE",EDGE,{"disambiguationData":[OSD([sQuery(id+"F24.wireOp",EDGE,"E69.0.1"),sQuery(id+"F24.wireOp",EDGE,"E69.0.2")])]});
            fillet(context, id + "F27", {"entities" : qUnion([Q0, Q1, Q2, Q3]), "radius" : 1 * mm, "tangentPropagation" : true, "allowEdgeOverflow" : false});
        }
        {
            var Q0;
            Q0=makeQuery(id+"F3.boolean.opBoolean","COPY",EDGE,{"derivedFrom":makeQuery(id+"F3.opExtrude","CAP_EDGE",EDGE,{"disambiguationData":[OSD([sQuery(id+"F2.wireOp",EDGE,"E8")])],"isStart":false})});
            var Q1;
            Q1=makeQuery(id+"F9.opExtrude","TWEAK_EDGE",EDGE,{"derivedFrom":[makeQuery(id+"F7.boolean.opBoolean","COPY",FACE,{"derivedFrom":makeQuery(id+"F7.opExtrude","SWEPT_FACE",FACE,{"disambiguationData":[OSD([sQuery(id+"F6.wireOp",EDGE,"E20.0")])]})}),makeQuery(id+"F8.imprint","IMPRINT",EDGE,{"derivedFrom":sQuery(id+"F8.wireOp",EDGE,"E27.top")})]});
            var Q2;
            Q2=makeQuery(id+"F9.opExtrude","CAP_EDGE",EDGE,{"disambiguationData":[OSD([sQuery(id+"F8.wireOp",EDGE,"E27.top")])],"isStart":true});
            var Q3;
            Q3=makeQuery(id+"F11.opExtrude","TWEAK_EDGE",EDGE,{"derivedFrom":[makeQuery(id+"F7.boolean.opBoolean","COPY",FACE,{"derivedFrom":makeQuery(id+"F7.opExtrude","SWEPT_FACE",FACE,{"disambiguationData":[OSD([sQuery(id+"F6.wireOp",EDGE,"E23.0")])]})}),makeQuery(id+"F10.imprint","IMPRINT",EDGE,{"derivedFrom":sQuery(id+"F10.wireOp",EDGE,"E29.top")})]});
            var Q4;
            Q4=makeQuery(id+"F11.opExtrude","CAP_EDGE",EDGE,{"disambiguationData":[OSD([sQuery(id+"F10.wireOp",EDGE,"E29.top")])],"isStart":true});
            var Q5;
            Q5=makeQuery(id+"FQgWeVVyTOw4oP8_1.1.F13.opExtrude","CAP_EDGE",EDGE,{"disambiguationData":[OSD([sQuery(id+"F12.wireOp",EDGE,"E35")])],"isStart":false});
            var Q6;
            Q6=makeQuery(id+"F13.opExtrude","CAP_EDGE",EDGE,{"disambiguationData":[OSD([sQuery(id+"F12.wireOp",EDGE,"E35")])],"isStart":false});
            fillet(context, id + "F28", {"entities" : qUnion([Q0, Q1, Q2, Q3, Q4, Q5, Q6]), "radius" : 1 * mm, "tangentPropagation" : true, "allowEdgeOverflow" : false});
        }
        {
            var Q0;
            Q0=makeQuery(id+"F3.boolean.opBoolean","COPY",EDGE,{"derivedFrom":makeQuery(id+"F3.opExtrude","SWEPT_EDGE",EDGE,{"disambiguationData":[OSD([sQuery(id+"F0.wireOp",EDGE,"E3"),sQuery(id+"F2.wireOp",EDGE,"E6"),sQuery(id+"F2.wireOp",EDGE,"E8")])]})});
            var Q1;
            Q1=makeQuery(id+"F13.opExtrude","SWEPT_EDGE",EDGE,{"disambiguationData":[OSD([sQuery(id+"F0.wireOp",EDGE,"E2.left"),sQuery(id+"F10.wireOp",EDGE,"E29.bottom"),sQuery(id+"F12.wireOp",EDGE,"E34"),sQuery(id+"F12.wireOp",EDGE,"E35")])]});
            var Q2;
            Q2=makeQuery(id+"F15.opExtrude","SWEPT_EDGE",EDGE,{"disambiguationData":[OSD([sQuery(id+"F0.wireOp",EDGE,"E2.bottom"),sQuery(id+"F8.wireOp",EDGE,"E27.bottom"),sQuery(id+"F14.wireOp",EDGE,"E43"),sQuery(id+"F14.wireOp",EDGE,"E45")])]});
            var Q3;
            Q3=makeQuery(id+"F13.opExtrude","SWEPT_EDGE",EDGE,{"disambiguationData":[OSD([sQuery(id+"F0.wireOp",EDGE,"E2.left"),sQuery(id+"F10.wireOp",EDGE,"E30.bottom"),sQuery(id+"F12.wireOp",EDGE,"0e25475b-3a4a-4502-b2ef-1a4ccfbb12352.MirrorCS"),sQuery(id+"F12.wireOp",EDGE,"0e25475b-3a4a-4502-b2ef-1a4ccfbb12354.MirrorCS")])]});
            var Q4;
            Q4=makeQuery(id+"F15.opExtrude","CAP_EDGE",EDGE,{"disambiguationData":[OSD([sQuery(id+"F14.wireOp",EDGE,"14d68a54-c34f-48c8-ae77-41faf57796822.MirrorCS")])],"isStart":false});
            var Q5;
            Q5=makeQuery(id+"F1.opExtrude","SWEPT_EDGE",EDGE,{"disambiguationData":[OSD([sQuery(id+"F0.wireOp",EDGE,"E2.bottom"),sQuery(id+"F0.wireOp",EDGE,"E2.right")])]});
            var Q6;
            Q6=makeQuery(id+"F1.opExtrude","SWEPT_EDGE",EDGE,{"disambiguationData":[OSD([sQuery(id+"F0.wireOp",EDGE,"E2.top"),sQuery(id+"F0.wireOp",EDGE,"E2.left")])]});
            var Q7;
            Q7=makeQuery(id+"F0G2RlgfnTVtGBU_1.1.F15.opExtrude","SWEPT_EDGE",EDGE,{"disambiguationData":[OSD([sQuery(id+"F0.wireOp",EDGE,"E2.bottom"),sQuery(id+"F8.wireOp",EDGE,"E27.bottom"),sQuery(id+"F14.wireOp",EDGE,"E43"),sQuery(id+"F14.wireOp",EDGE,"E45")])]});
            fillet(context, id + "F29", {"entities" : qUnion([Q0, Q1, Q2, Q3, Q4, Q5, Q6, Q7]), "radius" : 1 * mm, "tangentPropagation" : true, "allowEdgeOverflow" : false});
        }
        {
            var Q0;
            Q0=makeQuery(id+"F1.opExtrude","CAP_EDGE",EDGE,{"disambiguationData":[OSD([sQuery(id+"F0.wireOp",EDGE,"E2.top")])],"isStart":false});
            var Q1;
            Q1=makeQuery(id+"F3.boolean.opBoolean","COPY",EDGE,{"derivedFrom":makeQuery(id+"F3.opExtrude","CAP_EDGE",EDGE,{"disambiguationData":[OSD([sQuery(id+"F2.wireOp",EDGE,"E8")])],"isStart":true})});
            fillet(context, id + "F30", {"entities" : qUnion([Q0, Q1]), "radius" : 1 * mm, "tangentPropagation" : true, "allowEdgeOverflow" : false});
        }
    });
